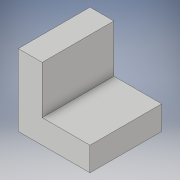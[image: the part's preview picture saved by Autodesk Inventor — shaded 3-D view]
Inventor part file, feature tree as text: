
AUTODESK INVENTOR PART (.ipt)
format: ipt  version: 2017 (Build 210142000, 142)  size: 90,624 bytes
history: native  units: in
note: dims shown in document units (in); Inventor stores cm internally (conversion verified against a paired STEP export)
features: extrude x1, sketch x1
ambient origin geometry x8: Origin, YZ Plane, XZ Plane, XY Plane, X Axis, Y Axis, Z Axis, Center Point
bodies: Solid1 (feature_tree)
feature tree (2):
  extrude  "Extrusion1"  Depth=0.5in
  sketch  "Sketch1"  dims[d0=1.5in d1=0.5in d2=1.0in d3=1.0in d4=1.5in d5=0.0in]
